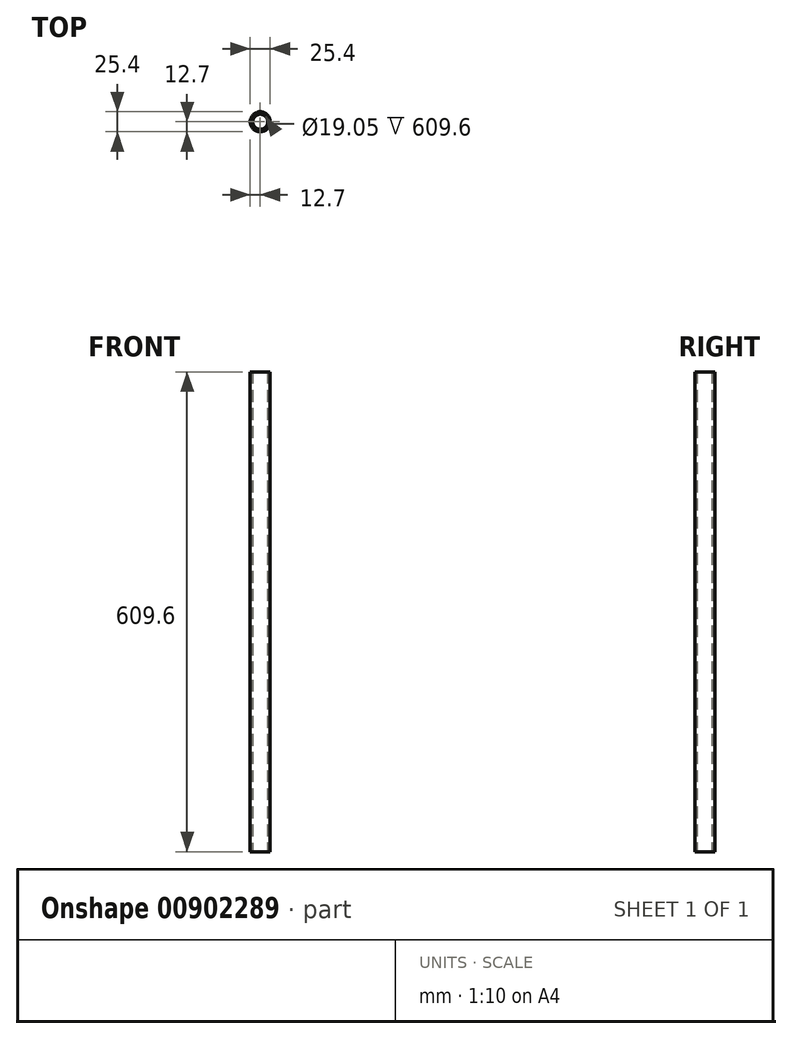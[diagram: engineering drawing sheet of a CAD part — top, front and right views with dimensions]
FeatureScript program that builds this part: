
annotation { "Feature Type Name" : "Feature", "Feature Type Description" : "" }
export const myFeature = defineFeature(function(context is Context, id is Id, definition is map)
    precondition{}
    {
        {
            var Q0;
            Q0=qCreatedBy(makeId("Top.planeOp"),FACE);
            var sketch = newSketch(context, id + "F0", { "sketchPlane" : qUnion([Q0])});
            skCircle(sketch, "E0", {"center": v(0, 0) * mm, "radius": 12.7 * mm});
            skSolve(sketch);
        }
        {
            var Q0;
            Q0=makeQuery(id+"F0.imprint","IMPRINT",FACE,{"disambiguationData":[TD([[makeQuery(id+"F0.imprint","IMPRINT",EDGE,{"derivedFrom":sQuery(id+"F0.wireOp",EDGE,"E0")}),1.0]])]});
            extrude(context, id + "F1", {"entities" : qUnion([Q0]), "depth" : 609.6 * mm, "offsetDistance" : 25.4 * mm});
        }
        {
            var Q0;
            Q0=qCreatedBy(makeId("Top.planeOp"),FACE);
            var sketch = newSketch(context, id + "F2", { "sketchPlane" : qUnion([Q0])});
            skPoint(sketch, "E1", {"position": v(0, 0) * mm});
            skSolve(sketch);
        }
        {
            var Q0;
            Q0=sQuery(id+"F2.wireOp",VERTEX,"E1");
            var Q1;
            Q1=makeQuery(id+"F1.opExtrude","SWEPT_BODY",BODY,{"disambiguationData":[OSD([sQuery(id+"F0.wireOp",EDGE,"E0")])]});
            hole(context, id + "F3", {"style" : HoleStyle.SIMPLE, "endStyle" : HoleEndStyle.THROUGH, "oppositeDirection" : true, "holeDiameter" : 19.05 * mm, "majorDiameter" : 6.35 * mm, "isTappedThrough" : true, "tappedDepth" : 12.7 * mm, "tapClearance" : 3, "locations" : qUnion([Q0]), "scope" : qUnion([Q1])});
        }
    });
